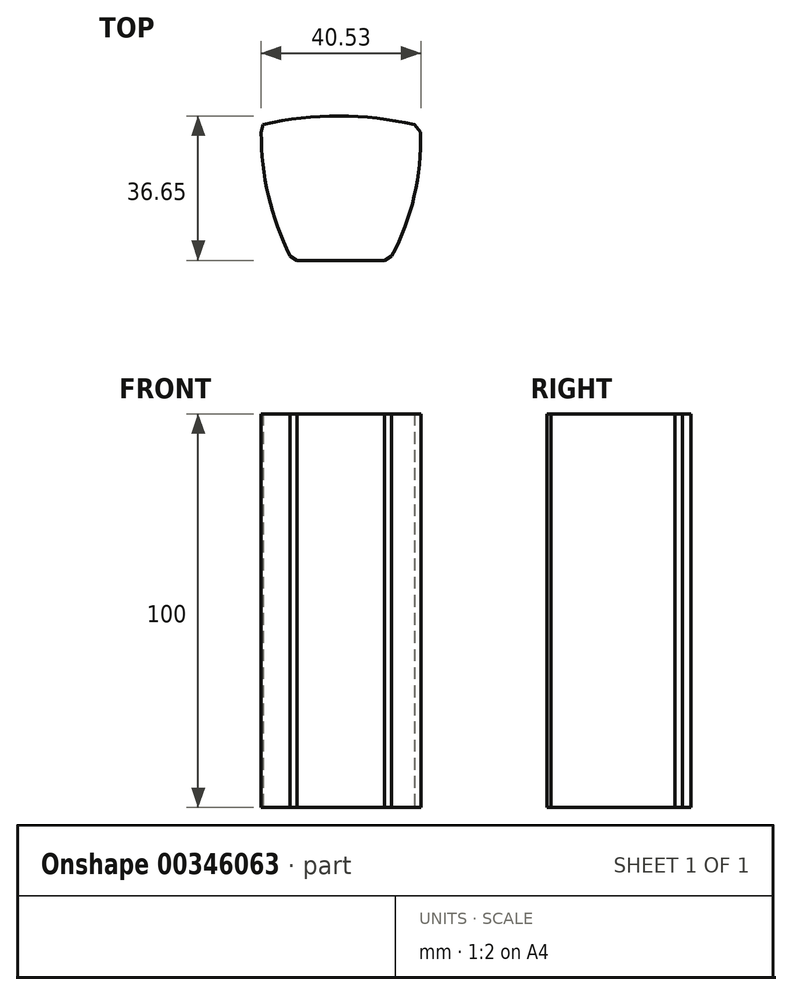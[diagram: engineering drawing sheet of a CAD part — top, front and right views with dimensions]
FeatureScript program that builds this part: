
annotation { "Feature Type Name" : "Feature", "Feature Type Description" : "" }
export const myFeature = defineFeature(function(context is Context, id is Id, definition is map)
    precondition{}
    {
        {
            var Q0;
            Q0=qCreatedBy(makeId("Top.planeOp"),FACE);
            var sketch = newSketch(context, id + "F0", { "sketchPlane" : qUnion([Q0])});
            skLineSegment(sketch, "E0", {"start": v(0, 0) * mm, "end": v(11.12, 0) * mm});
            skLineSegment(sketch, "E1", {"start": v(0, 0) * mm, "end": v(-11.12, 0) * mm});
            skArc(sketch, "E2", {"start": v(11.12, 0) * mm, "mid": v(16.67, 14.79) * mm, "end": v(18.25, 30.5) * mm});
            skArc(sketch, "E3", {"start": v(-18.25, 30.8) * mm, "mid": v(-16.5, 14.98) * mm, "end": v(-11.12, 0) * mm});
            skArc(sketch, "E4", {"start": v(18.25, 30.5) * mm, "mid": v(0.02, 32.65) * mm, "end": v(-18.25, 30.8) * mm});
            skArc(sketch, "E5.0", {"start": v(18.68, 32.45) * mm, "mid": v(-0.53, 34.65) * mm, "end": v(-19.74, 32.52) * mm});
            skArc(sketch, "E6.0", {"start": v(-20.25, 30.5) * mm, "mid": v(-18.41, 14.38) * mm, "end": v(-12.92, -0.9) * mm});
            skLineSegment(sketch, "E7.0", {"start": v(0, -2) * mm, "end": v(11.12, -2) * mm});
            skLineSegment(sketch, "E8.0", {"start": v(0, -2) * mm, "end": v(-11.13, -2) * mm});
            skArc(sketch, "E9.0", {"start": v(12.9, -0.94) * mm, "mid": v(18.62, 14.33) * mm, "end": v(20.25, 30.56) * mm});
            skLineSegment(sketch, "E10", {"start": v(-20.25, 30.5) * mm, "end": v(-19.74, 32.52) * mm});
            skLineSegment(sketch, "E11", {"start": v(18.68, 32.45) * mm, "end": v(20.25, 30.56) * mm});
            skLineSegment(sketch, "E12", {"start": v(12.9, -0.94) * mm, "end": v(11.12, -2) * mm});
            skLineSegment(sketch, "E13", {"start": v(-11.13, -2) * mm, "end": v(-12.92, -0.9) * mm});
            skSolve(sketch);
        }
        {
            var Q0;
            Q0=makeQuery(id+"F0.imprint","IMPRINT",FACE,{"disambiguationData":[TD([[makeQuery(id+"F0.imprint","IMPRINT",EDGE,{"derivedFrom":sQuery(id+"F0.wireOp",EDGE,"E0")}),-1.0]])]});
            var Q1;
            Q1=makeQuery(id+"F0.imprint","IMPRINT",FACE,{"disambiguationData":[TD([[makeQuery(id+"F0.imprint","IMPRINT",EDGE,{"derivedFrom":sQuery(id+"F0.wireOp",EDGE,"E0")}),1.0]])]});
            extrude(context, id + "F1", {"entities" : qUnion([Q0, Q1]), "depth" : 100 * mm});
        }
    });
